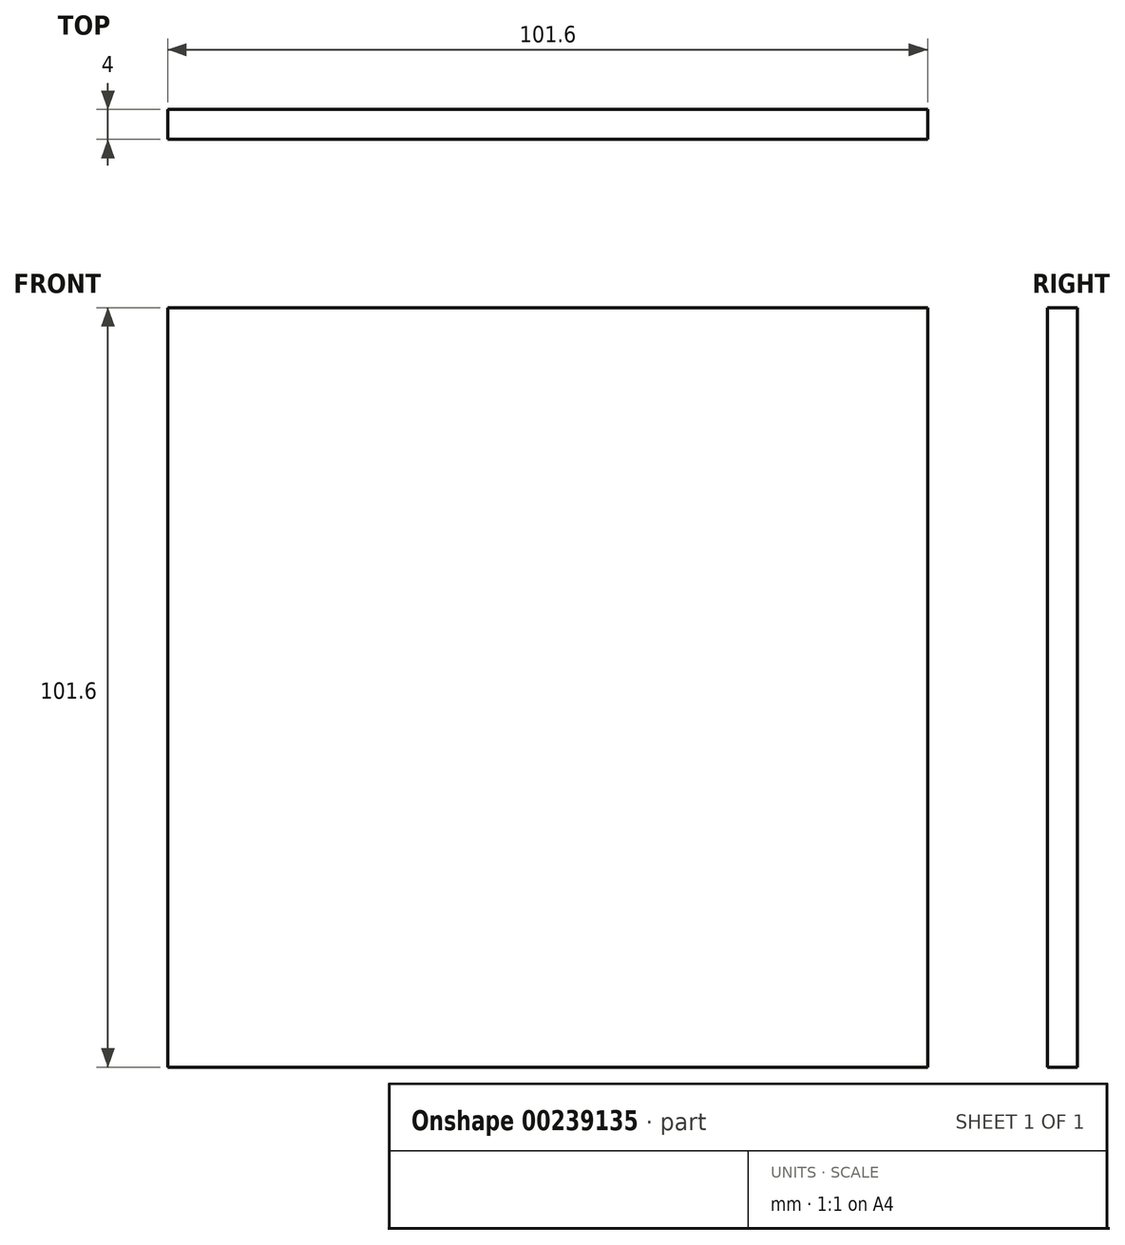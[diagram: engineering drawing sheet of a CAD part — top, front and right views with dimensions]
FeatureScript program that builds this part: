
annotation { "Feature Type Name" : "Feature", "Feature Type Description" : "" }
export const myFeature = defineFeature(function(context is Context, id is Id, definition is map)
    precondition{}
    {
        {
            assignVariable(context, id + "F0", {"name" : "S", "anyValue" : 4});
        }
        {
            var Q0;
            Q0=qCreatedBy(makeId("Front.planeOp"),FACE);
            var sketch = newSketch(context, id + "F1", { "sketchPlane" : qUnion([Q0])});
            skLineSegment(sketch, "E0.bottom", {"start": v(-50.8, 50.8) * mm, "end": v(50.8, 50.8) * mm});
            skLineSegment(sketch, "E0.top", {"start": v(-50.8, -50.8) * mm, "end": v(50.8, -50.8) * mm});
            skLineSegment(sketch, "E0.left", {"start": v(-50.8, 50.8) * mm, "end": v(-50.8, -50.8) * mm});
            skLineSegment(sketch, "E0.right", {"start": v(50.8, 50.8) * mm, "end": v(50.8, -50.8) * mm});
            skPoint(sketch, "E0.middle", {"position": v(0, 0) * mm});
            skSolve(sketch);
        }
        {
            var Q0;
            Q0=makeQuery(id+"F1.imprint","IMPRINT",FACE,{"disambiguationData":[TD([[makeQuery(id+"F1.imprint","IMPRINT",EDGE,{"derivedFrom":sQuery(id+"F1.wireOp",EDGE,"E0.bottom")}),-1.0]])]});
            extrude(context, id + "F2", {"entities" : qUnion([Q0]), "endBound" : BoundingType.SYMMETRIC, "depth" : (getVariable(context, 'S')) * mm});
        }
    });
